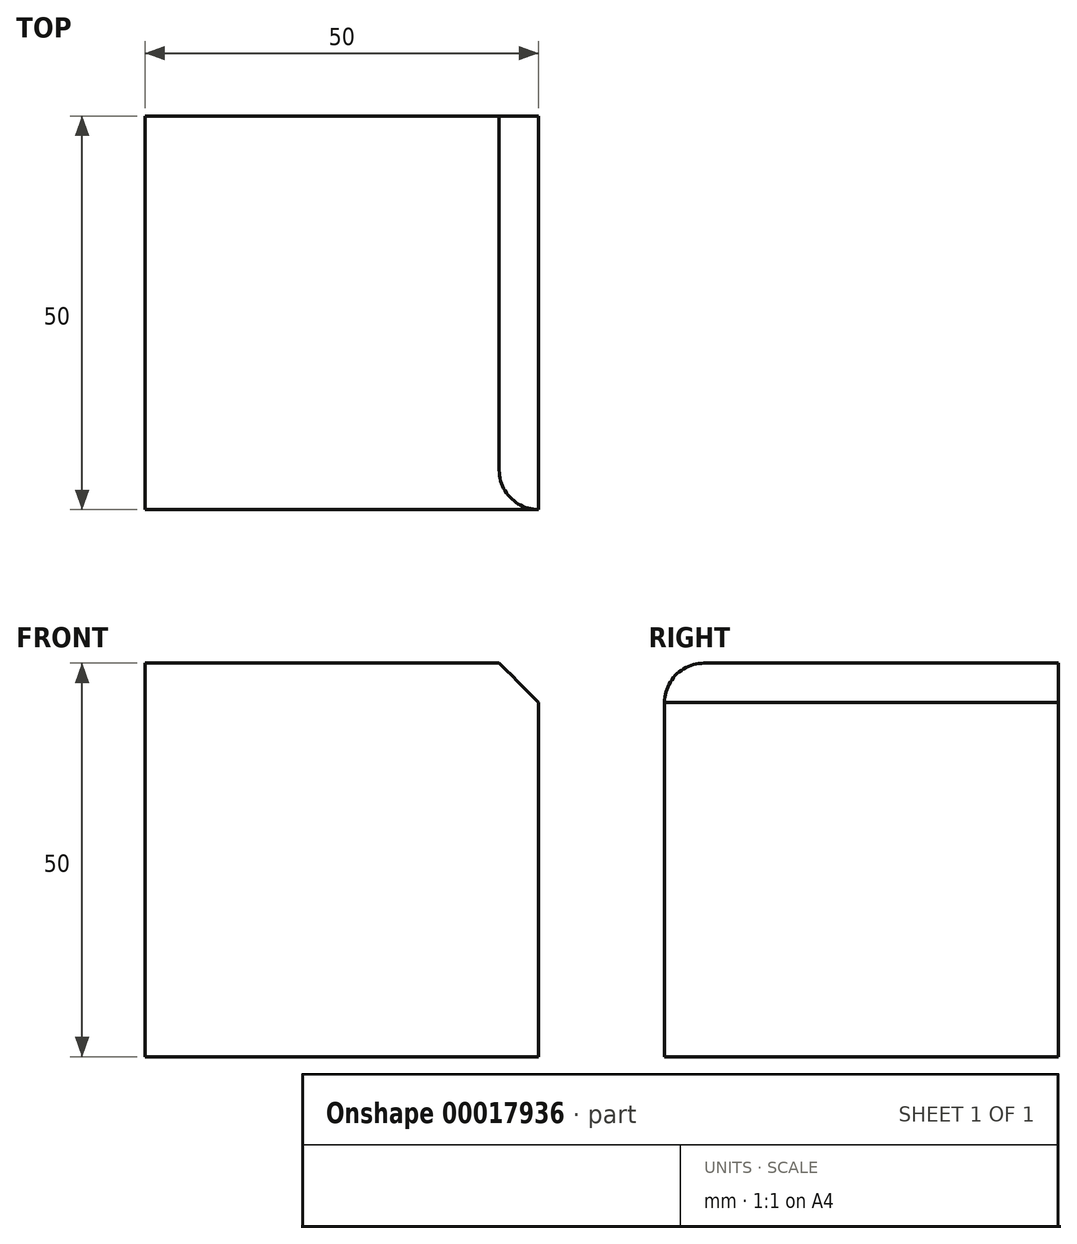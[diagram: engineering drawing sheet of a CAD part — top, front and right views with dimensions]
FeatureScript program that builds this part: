
annotation { "Feature Type Name" : "Feature", "Feature Type Description" : "" }
export const myFeature = defineFeature(function(context is Context, id is Id, definition is map)
    precondition{}
    {
        {
            var Q0;
            Q0=qCreatedBy(makeId("Top.planeOp"),FACE);
            var sketch = newSketch(context, id + "F0", { "sketchPlane" : qUnion([Q0])});
            skLineSegment(sketch, "E0.rect.bottom", {"start": v(-25, 25) * mm, "end": v(25, 25) * mm});
            skLineSegment(sketch, "E0.rect.top", {"start": v(-25, -25) * mm, "end": v(25, -25) * mm});
            skLineSegment(sketch, "E0.rect.left", {"start": v(-25, 25) * mm, "end": v(-25, -25) * mm});
            skLineSegment(sketch, "E0.rect.right", {"start": v(25, 25) * mm, "end": v(25, -25) * mm});
            skPoint(sketch, "E0.rect.middle", {"position": v(0, 0) * mm});
            skSolve(sketch);
        }
        {
            var Q0;
            Q0=makeQuery(id+"F0.imprint","IMPRINT",FACE,{"disambiguationData":[TD([[makeQuery(id+"F0.imprint","IMPRINT",EDGE,{"derivedFrom":sQuery(id+"F0.wireOp",EDGE,"E0.rect.bottom")}),-1.0]])]});
            extrude(context, id + "F1", {"entities" : qUnion([Q0]), "depth" : 50 * mm});
        }
        {
            var Q0;
            Q0=makeQuery(id+"F1.opExtrude","CAP_EDGE",EDGE,{"disambiguationData":[OSD([sQuery(id+"F0.wireOp",EDGE,"E0.rect.right")])],"isStart":false});
            chamfer(context, id + "F2", {"entities" : qUnion([Q0]), "width" : 5 * mm, "tangentPropagation" : true});
        }
        {
            var Q0;
            Q0=makeQuery(id+"F1.opExtrude","CAP_EDGE",EDGE,{"disambiguationData":[OSD([sQuery(id+"F0.wireOp",EDGE,"E0.rect.top")])],"isStart":false});
            fillet(context, id + "F3", {"entities" : qUnion([Q0]), "radius" : 5 * mm, "tangentPropagation" : true, "allowEdgeOverflow" : false});
        }
    });
